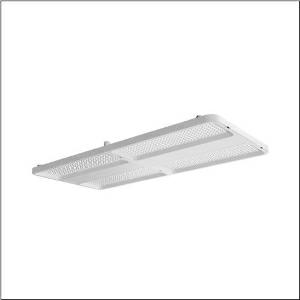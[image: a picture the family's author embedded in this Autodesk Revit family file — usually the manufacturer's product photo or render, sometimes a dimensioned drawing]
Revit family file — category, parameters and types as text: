
# Revit family: highbay_11_maxi_51hn11db4qda
name_source: partatom
category: Lighting Fixtures
units: mm (PartAtom-declared; Revit-internal decimal feet)

## family parameters
Cut with Voids When Loaded = No
Host = Face
Light Source = No
Part Type = Normal
Room Calculation Point = No
Round Connector Dimension = Use Diameter
Shared = No

## types (1)
- --- (1 x LED, 5620 lm, 27.8 W, 4000K)
    Apparent Load = 28 VA
    CIE Flux Codes = 85 97 100 100 100
    Color Rendering = 80
    Color Temperature = 4000K
    Default Elevation = 1800 mm
    Description = high bay luminaire Highbay 11 maxi; direct symmetric narrow distribution, light control with lens of PMMA; UGR ≤ 22 (X = 4H | Y = 8H | S = 0.25H | reflection values 70/50/20); luminous flux: 36.000lm; light colour: 840, colour temperature: 4000K, MacAdam ≤ 2 SDCM (initial), colour rendering: CRI > 80; luminous efficacy: 202,6lm/W; rated service life: 100.000h (L95/B50) at AT= 25°C; control: DALI 2; luminaire connection: terminal, 5-pole, max. 2.5mm² (cable entry for one cable, Ø 8.5..16mm); mains connection: 230..240V, AC/DC 0/50..60Hz; connected load: 177,7W; protection rating (complete): IP66; insulation class (complete): insulation class I (protective earthing); protection symbol: D; impact resistance: IK08; certification: CE, ENEC, VDE, UKCA; luminaire for central battery installations according to DIN EN 60598-2-22, internal wiring halogen-free; luminaire corresponds to IFS (International Featured Standards) requirements for safety and quality in the food industry; LABS conformity tested according to VDMA 24364:2018-05; housing frame of high-performance plastic PA6, matt traffic white (RAL 9016); cover of PMMA; dimension (LxWxH): 946 x 442 x 72mm; permissible operating ambient temperature: -40..+55°C (reducing of maximum allowable ambient temperature of 5°C with ceiling mounting); packaging unit: 1 piece; (delivery without accessories; please order mounting accessories separately)
    Height = 72 mm  [stored 0.23622 ft]
    Lamp = 1 x LED
    Lamp Light Flux = 5620 lm
    Lamp Power = 27.8 W
    Lamp count = 1
    Length = 946 mm
    Luminous efficacy = 202 lm/W
    Manufacturer = Siteco
    ModVariant = No
    Model = 51HN11DB4QDA
    Mounting Place = Ceiling
    Mounting Type = Pendant
    Number of Poles = 1
    OnlyDefault = Yes
    Power Factor = 1
    Product Name = Highbay 11 maxi
    Product group = high bay luminaire
    ProductGroupID = 901
    Protection Class = Protection class I
    Protection Degree = IP 66
    RLX_Detail_Level = 1
    RLX_Emergency_Light_Flux = 0 lm
    RLX_Emergency_Type = 0
    RLX_Emergency_Type_DB = No
    RlxData = <blob elided: 127761 chars, md5=eb62c0c3>
    Socket = socket
    Standby Power = 0 W
    System Light Flux = 5620 lm
    System Power = 28 W
    Type Comments = : DC mode (central or group accumulator) initial emergency light level
    Type Image = l_1363244.jpg
    URL = http://relux.com
    VarID = @adj_021039
    Voltage = 0 V
    Weight = 0.00 kg
    Width = 442 mm

note: [stored X ft] marks values corroborated as IEEE doubles in the binary element streams (Revit-internal decimal feet)

## geometry (parser evidence)
native form markers: Blend x4, Sweep x10
no freeform markers — native parametric forms only
